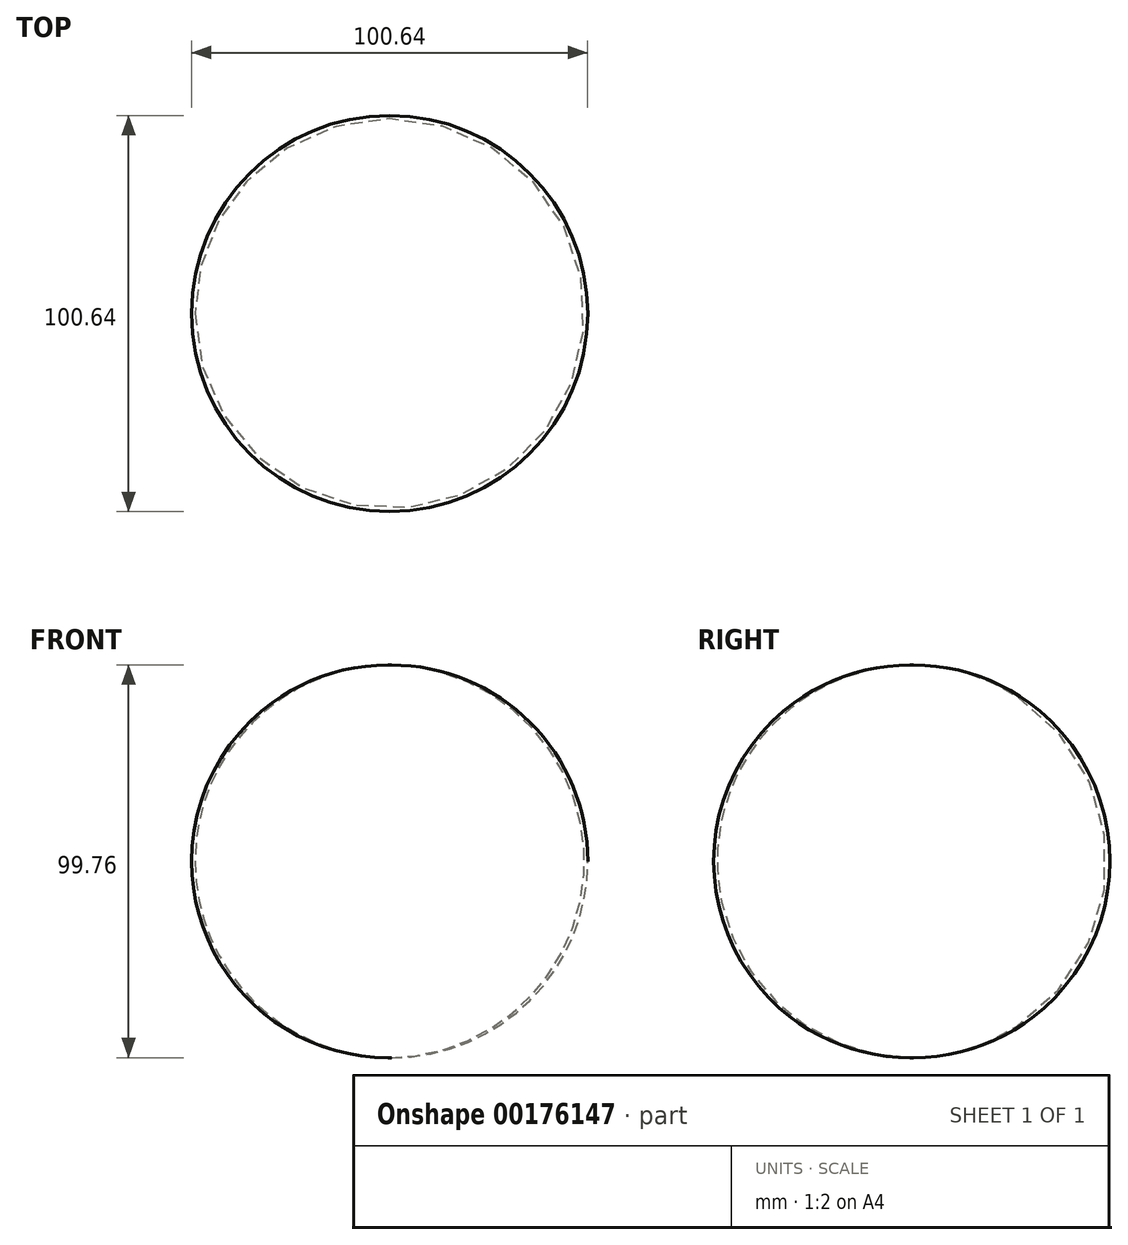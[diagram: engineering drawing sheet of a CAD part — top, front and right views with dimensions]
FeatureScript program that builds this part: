
annotation { "Feature Type Name" : "Feature", "Feature Type Description" : "" }
export const myFeature = defineFeature(function(context is Context, id is Id, definition is map)
    precondition{}
    {
        {
            var Q0;
            Q0=qCreatedBy(makeId("Front.planeOp"),FACE);
            var sketch = newSketch(context, id + "F0", { "sketchPlane" : qUnion([Q0])});
            skLineSegment(sketch, "E0", {"start": v(0, 53.94) * mm, "end": v(0, -45.82) * mm});
            skArc(sketch, "E1", {"start": v(0, -45.82) * mm, "mid": v(49.44, 4.06) * mm, "end": v(0, 53.94) * mm});
            skSolve(sketch);
        }
        {
            var Q0;
            Q0=makeQuery(id+"F0.imprint","IMPRINT",FACE,{"disambiguationData":[TD([[makeQuery(id+"F0.imprint","IMPRINT",EDGE,{"derivedFrom":sQuery(id+"F0.wireOp",EDGE,"E0")}),1.0]])]});
            var Q1;
            Q1=sQuery(id+"F0.wireOp",EDGE,"E0");
            revolve(context, id + "F1", {"entities" : qUnion([Q0]), "axis" : qUnion([Q1]), "revolveType" : RevolveType.FULL});
        }
    });
